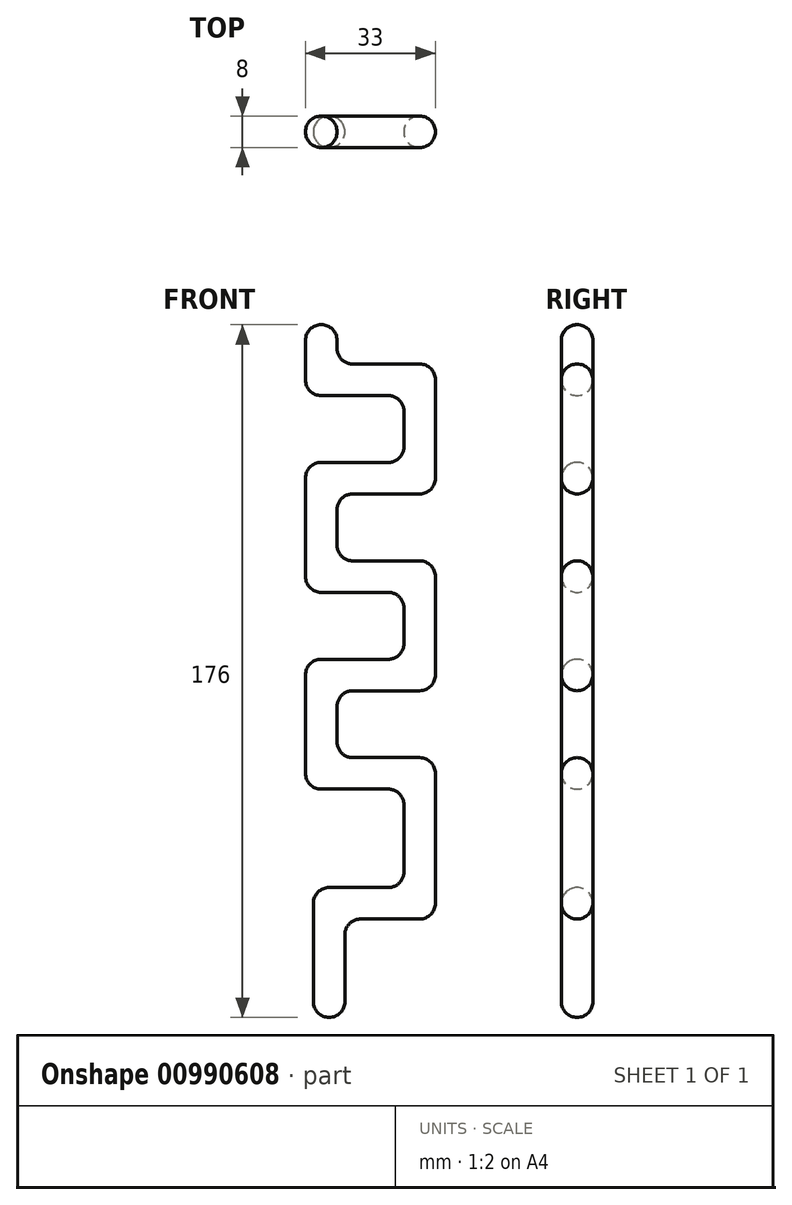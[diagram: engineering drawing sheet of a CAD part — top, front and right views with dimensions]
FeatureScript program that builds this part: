
annotation { "Feature Type Name" : "Feature", "Feature Type Description" : "" }
export const myFeature = defineFeature(function(context is Context, id is Id, definition is map)
    precondition{}
    {
        {
            var Q0;
            Q0=qCreatedBy(makeId("Top.planeOp"),FACE);
            var sketch = newSketch(context, id + "F0", { "sketchPlane" : qUnion([Q0])});
            skLineSegment(sketch, "E0.bottom", {"start": v(-57.93, 3.33) * mm, "end": v(-49.93, 3.33) * mm});
            skLineSegment(sketch, "E0.top", {"start": v(-57.93, -4.67) * mm, "end": v(-49.93, -4.67) * mm});
            skLineSegment(sketch, "E0.left", {"start": v(-57.93, 3.33) * mm, "end": v(-57.93, -4.67) * mm});
            skLineSegment(sketch, "E0.right", {"start": v(-49.93, 3.33) * mm, "end": v(-49.93, -4.67) * mm});
            skSolve(sketch);
        }
        {
            var Q0;
            Q0 = qSketchRegion(id + "F0", true);
            extrude(context, id + "F1", {"entities" : qUnion([Q0]), "depth" : 33 * mm, "offsetDistance" : 25 * mm});
        }
        {
            var Q0;
            Q0=makeQuery(id+"F1.opExtrude","SWEPT_FACE",FACE,{"disambiguationData":[OSD([sQuery(id+"F0.wireOp",EDGE,"E0.right")])]});
            var sketch = newSketch(context, id + "F2", { "sketchPlane" : qUnion([Q0])});
            skLineSegment(sketch, "E1.bottom", {"start": v(3.33, 33) * mm, "end": v(-4.67, 33) * mm});
            skLineSegment(sketch, "E1.top", {"start": v(3.33, 25) * mm, "end": v(-4.67, 25) * mm});
            skLineSegment(sketch, "E1.left", {"start": v(3.33, 33) * mm, "end": v(3.33, 25) * mm});
            skLineSegment(sketch, "E1.right", {"start": v(-4.67, 33) * mm, "end": v(-4.67, 25) * mm});
            skSolve(sketch);
        }
        {
            var Q0;
            Q0 = qSketchRegion(id + "F2", true);
            extrude(context, id + "F3", {"entities" : qUnion([Q0]), "operationType" : NewBodyOperationType.ADD, "depth" : 23 * mm, "offsetDistance" : 25 * mm});
        }
        {
            var Q0;
            Q0=makeQuery(id+"F3.opExtrude","SWEPT_FACE",FACE,{"disambiguationData":[OSD([sQuery(id+"F2.wireOp",EDGE,"E1.top")])]});
            var sketch = newSketch(context, id + "F4", { "sketchPlane" : qUnion([Q0])});
            skLineSegment(sketch, "E2.bottom", {"start": v(-26.93, 4.67) * mm, "end": v(-34.93, 4.67) * mm});
            skLineSegment(sketch, "E2.top", {"start": v(-26.93, -3.33) * mm, "end": v(-34.93, -3.33) * mm});
            skLineSegment(sketch, "E2.left", {"start": v(-26.93, 4.67) * mm, "end": v(-26.93, -3.33) * mm});
            skLineSegment(sketch, "E2.right", {"start": v(-34.93, 4.67) * mm, "end": v(-34.93, -3.33) * mm});
            skSolve(sketch);
        }
        {
            var Q0;
            Q0 = qSketchRegion(id + "F4", true);
            extrude(context, id + "F5", {"entities" : qUnion([Q0]), "operationType" : NewBodyOperationType.ADD, "oppositeDirection" : true, "depth" : 41 * mm, "offsetDistance" : 25 * mm});
        }
        {
            var Q0;
            Q0=makeQuery(id+"F5.opExtrude","SWEPT_FACE",FACE,{"disambiguationData":[OSD([sQuery(id+"F4.wireOp",EDGE,"E2.right")])]});
            var sketch = newSketch(context, id + "F6", { "sketchPlane" : qUnion([Q0])});
            skLineSegment(sketch, "E3.bottom", {"start": v(-3.33, 66) * mm, "end": v(4.67, 66) * mm});
            skLineSegment(sketch, "E3.top", {"start": v(-3.33, 58) * mm, "end": v(4.67, 58) * mm});
            skLineSegment(sketch, "E3.left", {"start": v(-3.33, 66) * mm, "end": v(-3.33, 58) * mm});
            skLineSegment(sketch, "E3.right", {"start": v(4.67, 66) * mm, "end": v(4.67, 58) * mm});
            skSolve(sketch);
        }
        {
            var Q0;
            Q0 = qSketchRegion(id + "F6", true);
            extrude(context, id + "F7", {"entities" : qUnion([Q0]), "operationType" : NewBodyOperationType.ADD, "depth" : 25 * mm, "offsetDistance" : 25 * mm});
        }
        {
            var Q0;
            Q0=makeQuery(id+"F7.boolean.opBoolean","MERGE",FACE,{"derivedFrom":[makeQuery(id+"F5.opExtrude","CAP_FACE",FACE,{"disambiguationData":[OSD([sQuery(id+"F4.wireOp",EDGE,"E2.bottom"),sQuery(id+"F4.wireOp",EDGE,"E2.top"),sQuery(id+"F4.wireOp",EDGE,"E2.left"),sQuery(id+"F4.wireOp",EDGE,"E2.right")])],"isStart":false}),makeQuery(id+"F7.opExtrude","SWEPT_FACE",FACE,{"disambiguationData":[OSD([sQuery(id+"F6.wireOp",EDGE,"E3.bottom")])]})]});
            var sketch = newSketch(context, id + "F8", { "sketchPlane" : qUnion([Q0])});
            skLineSegment(sketch, "E4.bottom", {"start": v(-59.93, -4.67) * mm, "end": v(-51.93, -4.67) * mm});
            skLineSegment(sketch, "E4.top", {"start": v(-59.93, 3.33) * mm, "end": v(-51.93, 3.33) * mm});
            skLineSegment(sketch, "E4.left", {"start": v(-59.93, -4.67) * mm, "end": v(-59.93, 3.33) * mm});
            skLineSegment(sketch, "E4.right", {"start": v(-51.93, -4.67) * mm, "end": v(-51.93, 3.33) * mm});
            skSolve(sketch);
        }
        {
            var Q0;
            Q0 = qSketchRegion(id + "F8", true);
            extrude(context, id + "F9", {"entities" : qUnion([Q0]), "operationType" : NewBodyOperationType.ADD, "depth" : 25 * mm, "offsetDistance" : 25 * mm});
        }
        {
            var Q0;
            Q0=makeQuery(id+"F9.opExtrude","SWEPT_FACE",FACE,{"disambiguationData":[OSD([sQuery(id+"F8.wireOp",EDGE,"E4.right")])]});
            var sketch = newSketch(context, id + "F10", { "sketchPlane" : qUnion([Q0])});
            skLineSegment(sketch, "E5.bottom", {"start": v(-4.67, 91) * mm, "end": v(3.33, 91) * mm});
            skLineSegment(sketch, "E5.top", {"start": v(-4.67, 83) * mm, "end": v(3.33, 83) * mm});
            skLineSegment(sketch, "E5.left", {"start": v(-4.67, 91) * mm, "end": v(-4.67, 83) * mm});
            skLineSegment(sketch, "E5.right", {"start": v(3.33, 91) * mm, "end": v(3.33, 83) * mm});
            skSolve(sketch);
        }
        {
            var Q0;
            Q0 = qSketchRegion(id + "F10", true);
            extrude(context, id + "F11", {"entities" : qUnion([Q0]), "operationType" : NewBodyOperationType.ADD, "depth" : 25 * mm, "offsetDistance" : 25 * mm});
        }
        {
            var Q0;
            Q0=makeQuery(id+"F11.boolean.opBoolean","MERGE",FACE,{"derivedFrom":[makeQuery(id+"F9.opExtrude","CAP_FACE",FACE,{"disambiguationData":[OSD([sQuery(id+"F8.wireOp",EDGE,"E4.bottom"),sQuery(id+"F8.wireOp",EDGE,"E4.top"),sQuery(id+"F8.wireOp",EDGE,"E4.left"),sQuery(id+"F8.wireOp",EDGE,"E4.right")])],"isStart":false}),makeQuery(id+"F11.opExtrude","SWEPT_FACE",FACE,{"disambiguationData":[OSD([sQuery(id+"F10.wireOp",EDGE,"E5.bottom")])]})]});
            var sketch = newSketch(context, id + "F12", { "sketchPlane" : qUnion([Q0])});
            skLineSegment(sketch, "E6.bottom", {"start": v(-26.93, 3.33) * mm, "end": v(-34.93, 3.33) * mm});
            skLineSegment(sketch, "E6.top", {"start": v(-26.93, -4.67) * mm, "end": v(-34.93, -4.67) * mm});
            skLineSegment(sketch, "E6.left", {"start": v(-26.93, 3.33) * mm, "end": v(-26.93, -4.67) * mm});
            skLineSegment(sketch, "E6.right", {"start": v(-34.93, 3.33) * mm, "end": v(-34.93, -4.67) * mm});
            skSolve(sketch);
        }
        {
            var Q0;
            Q0 = qSketchRegion(id + "F12", true);
            extrude(context, id + "F13", {"entities" : qUnion([Q0]), "operationType" : NewBodyOperationType.ADD, "depth" : 25 * mm, "offsetDistance" : 25 * mm});
        }
        {
            var Q0;
            Q0=makeQuery(id+"F13.opExtrude","SWEPT_FACE",FACE,{"disambiguationData":[OSD([sQuery(id+"F12.wireOp",EDGE,"E6.right")])]});
            var sketch = newSketch(context, id + "F14", { "sketchPlane" : qUnion([Q0])});
            skLineSegment(sketch, "E7.bottom", {"start": v(-3.33, 116) * mm, "end": v(4.67, 116) * mm});
            skLineSegment(sketch, "E7.top", {"start": v(-3.33, 108) * mm, "end": v(4.67, 108) * mm});
            skLineSegment(sketch, "E7.left", {"start": v(-3.33, 116) * mm, "end": v(-3.33, 108) * mm});
            skLineSegment(sketch, "E7.right", {"start": v(4.67, 116) * mm, "end": v(4.67, 108) * mm});
            skSolve(sketch);
        }
        {
            var Q0;
            Q0 = qSketchRegion(id + "F14", true);
            extrude(context, id + "F15", {"entities" : qUnion([Q0]), "operationType" : NewBodyOperationType.ADD, "depth" : 25 * mm, "offsetDistance" : 25 * mm});
        }
        {
            var Q0;
            Q0=makeQuery(id+"F15.boolean.opBoolean","MERGE",FACE,{"derivedFrom":[makeQuery(id+"F13.opExtrude","CAP_FACE",FACE,{"disambiguationData":[OSD([sQuery(id+"F12.wireOp",EDGE,"E6.bottom"),sQuery(id+"F12.wireOp",EDGE,"E6.top"),sQuery(id+"F12.wireOp",EDGE,"E6.left"),sQuery(id+"F12.wireOp",EDGE,"E6.right")])],"isStart":false}),makeQuery(id+"F15.opExtrude","SWEPT_FACE",FACE,{"disambiguationData":[OSD([sQuery(id+"F14.wireOp",EDGE,"E7.bottom")])]})]});
            var sketch = newSketch(context, id + "F16", { "sketchPlane" : qUnion([Q0])});
            skLineSegment(sketch, "E8.bottom", {"start": v(-59.93, -4.67) * mm, "end": v(-51.93, -4.67) * mm});
            skLineSegment(sketch, "E8.top", {"start": v(-59.93, 3.33) * mm, "end": v(-51.93, 3.33) * mm});
            skLineSegment(sketch, "E8.left", {"start": v(-59.93, -4.67) * mm, "end": v(-59.93, 3.33) * mm});
            skLineSegment(sketch, "E8.right", {"start": v(-51.93, -4.67) * mm, "end": v(-51.93, 3.33) * mm});
            skSolve(sketch);
        }
        {
            var Q0;
            Q0 = qSketchRegion(id + "F16", true);
            extrude(context, id + "F17", {"entities" : qUnion([Q0]), "operationType" : NewBodyOperationType.ADD, "depth" : 25 * mm, "offsetDistance" : 25 * mm});
        }
        {
            var Q0;
            Q0=makeQuery(id+"F17.opExtrude","SWEPT_FACE",FACE,{"disambiguationData":[OSD([sQuery(id+"F16.wireOp",EDGE,"E8.right")])]});
            var sketch = newSketch(context, id + "F18", { "sketchPlane" : qUnion([Q0])});
            skLineSegment(sketch, "E9.bottom", {"start": v(-4.67, 141) * mm, "end": v(3.33, 141) * mm});
            skLineSegment(sketch, "E9.top", {"start": v(-4.67, 133) * mm, "end": v(3.33, 133) * mm});
            skLineSegment(sketch, "E9.left", {"start": v(-4.67, 141) * mm, "end": v(-4.67, 133) * mm});
            skLineSegment(sketch, "E9.right", {"start": v(3.33, 141) * mm, "end": v(3.33, 133) * mm});
            skSolve(sketch);
        }
        {
            var Q0;
            Q0 = qSketchRegion(id + "F18", true);
            extrude(context, id + "F19", {"entities" : qUnion([Q0]), "operationType" : NewBodyOperationType.ADD, "depth" : 25 * mm, "offsetDistance" : 25 * mm});
        }
        {
            var Q0;
            Q0=makeQuery(id+"F19.boolean.opBoolean","MERGE",FACE,{"derivedFrom":[makeQuery(id+"F17.opExtrude","CAP_FACE",FACE,{"disambiguationData":[OSD([sQuery(id+"F16.wireOp",EDGE,"E8.bottom"),sQuery(id+"F16.wireOp",EDGE,"E8.top"),sQuery(id+"F16.wireOp",EDGE,"E8.left"),sQuery(id+"F16.wireOp",EDGE,"E8.right")])],"isStart":false}),makeQuery(id+"F19.opExtrude","SWEPT_FACE",FACE,{"disambiguationData":[OSD([sQuery(id+"F18.wireOp",EDGE,"E9.bottom")])]})]});
            var sketch = newSketch(context, id + "F20", { "sketchPlane" : qUnion([Q0])});
            skLineSegment(sketch, "E10.bottom", {"start": v(-26.93, 3.33) * mm, "end": v(-34.93, 3.33) * mm});
            skLineSegment(sketch, "E10.top", {"start": v(-26.93, -4.67) * mm, "end": v(-34.93, -4.67) * mm});
            skLineSegment(sketch, "E10.left", {"start": v(-26.93, 3.33) * mm, "end": v(-26.93, -4.67) * mm});
            skLineSegment(sketch, "E10.right", {"start": v(-34.93, 3.33) * mm, "end": v(-34.93, -4.67) * mm});
            skSolve(sketch);
        }
        {
            var Q0;
            Q0 = qSketchRegion(id + "F20", true);
            extrude(context, id + "F21", {"entities" : qUnion([Q0]), "operationType" : NewBodyOperationType.ADD, "depth" : 25 * mm, "offsetDistance" : 25 * mm});
        }
        {
            var Q0;
            Q0=makeQuery(id+"F21.opExtrude","SWEPT_FACE",FACE,{"disambiguationData":[OSD([sQuery(id+"F20.wireOp",EDGE,"E10.right")])]});
            var sketch = newSketch(context, id + "F22", { "sketchPlane" : qUnion([Q0])});
            skLineSegment(sketch, "E11.bottom", {"start": v(4.67, 166) * mm, "end": v(-3.33, 166) * mm});
            skLineSegment(sketch, "E11.top", {"start": v(4.67, 158) * mm, "end": v(-3.33, 158) * mm});
            skLineSegment(sketch, "E11.left", {"start": v(4.67, 166) * mm, "end": v(4.67, 158) * mm});
            skLineSegment(sketch, "E11.right", {"start": v(-3.33, 166) * mm, "end": v(-3.33, 158) * mm});
            skSolve(sketch);
        }
        {
            var Q0;
            Q0 = qSketchRegion(id + "F22", true);
            extrude(context, id + "F23", {"entities" : qUnion([Q0]), "operationType" : NewBodyOperationType.ADD, "depth" : 25 * mm, "offsetDistance" : 25 * mm});
        }
        {
            var Q0;
            Q0=makeQuery(id+"F23.boolean.opBoolean","MERGE",FACE,{"derivedFrom":[makeQuery(id+"F21.opExtrude","CAP_FACE",FACE,{"disambiguationData":[OSD([sQuery(id+"F20.wireOp",EDGE,"E10.bottom"),sQuery(id+"F20.wireOp",EDGE,"E10.top"),sQuery(id+"F20.wireOp",EDGE,"E10.left"),sQuery(id+"F20.wireOp",EDGE,"E10.right")])],"isStart":false}),makeQuery(id+"F23.opExtrude","SWEPT_FACE",FACE,{"disambiguationData":[OSD([sQuery(id+"F22.wireOp",EDGE,"E11.bottom")])]})]});
            var sketch = newSketch(context, id + "F24", { "sketchPlane" : qUnion([Q0])});
            skLineSegment(sketch, "E12.bottom", {"start": v(-59.93, -4.67) * mm, "end": v(-51.93, -4.67) * mm});
            skLineSegment(sketch, "E12.top", {"start": v(-59.93, 3.33) * mm, "end": v(-51.93, 3.33) * mm});
            skLineSegment(sketch, "E12.left", {"start": v(-59.93, -4.67) * mm, "end": v(-59.93, 3.33) * mm});
            skLineSegment(sketch, "E12.right", {"start": v(-51.93, -4.67) * mm, "end": v(-51.93, 3.33) * mm});
            skSolve(sketch);
        }
        {
            var Q0;
            Q0 = qSketchRegion(id + "F24", true);
            extrude(context, id + "F25", {"entities" : qUnion([Q0]), "operationType" : NewBodyOperationType.ADD, "depth" : 10 * mm, "offsetDistance" : 25 * mm});
        }
        {
            var Q0;
            Q0=makeQuery(id+"F3.opExtrude","SWEPT_EDGE",EDGE,{"disambiguationData":[OSD([sQuery(id+"F0.wireOp",EDGE,"E0.bottom"),sQuery(id+"F0.wireOp",EDGE,"E0.right"),sQuery(id+"F2.wireOp",EDGE,"E1.top"),sQuery(id+"F2.wireOp",EDGE,"E1.left")])]});
            var Q1;
            Q1=makeQuery(id+"F3.boolean.opBoolean","MERGE",EDGE,{"derivedFrom":[makeQuery(id+"F1.opExtrude","CAP_EDGE",EDGE,{"disambiguationData":[OSD([sQuery(id+"F0.wireOp",EDGE,"E0.top")])],"isStart":false}),makeQuery(id+"F3.opExtrude","SWEPT_EDGE",EDGE,{"disambiguationData":[OSD([sQuery(id+"F2.wireOp",EDGE,"E1.bottom"),sQuery(id+"F2.wireOp",EDGE,"E1.right")])]})]});
            var Q2;
            Q2=makeQuery(id+"F13.boolean.opBoolean","MERGE",FACE,{"derivedFrom":[makeQuery(id+"F11.opExtrude","CAP_FACE",FACE,{"disambiguationData":[OSD([sQuery(id+"F10.wireOp",EDGE,"E5.bottom"),sQuery(id+"F10.wireOp",EDGE,"E5.top"),sQuery(id+"F10.wireOp",EDGE,"E5.left"),sQuery(id+"F10.wireOp",EDGE,"E5.right")])],"isStart":false}),makeQuery(id+"F13.opExtrude","SWEPT_FACE",FACE,{"disambiguationData":[OSD([sQuery(id+"F12.wireOp",EDGE,"E6.left")])]})]});
            var Q3;
            Q3=makeQuery(id+"F13.opExtrude","SWEPT_EDGE",EDGE,{"disambiguationData":[OSD([sQuery(id+"F8.wireOp",EDGE,"E4.bottom"),sQuery(id+"F10.wireOp",EDGE,"E5.bottom"),sQuery(id+"F10.wireOp",EDGE,"E5.left"),sQuery(id+"F12.wireOp",EDGE,"E6.top"),sQuery(id+"F12.wireOp",EDGE,"E6.right")])]});
            var Q4;
            Q4=makeQuery(id+"F17.boolean.opBoolean","MERGE",FACE,{"derivedFrom":[makeQuery(id+"F15.opExtrude","CAP_FACE",FACE,{"disambiguationData":[OSD([sQuery(id+"F14.wireOp",EDGE,"E7.bottom"),sQuery(id+"F14.wireOp",EDGE,"E7.top"),sQuery(id+"F14.wireOp",EDGE,"E7.left"),sQuery(id+"F14.wireOp",EDGE,"E7.right")])],"isStart":false}),makeQuery(id+"F17.opExtrude","SWEPT_FACE",FACE,{"disambiguationData":[OSD([sQuery(id+"F16.wireOp",EDGE,"E8.left")])]})]});
            var Q5;
            Q5=makeQuery(id+"F7.opExtrude","SWEPT_EDGE",EDGE,{"disambiguationData":[OSD([sQuery(id+"F0.wireOp",EDGE,"E0.top"),sQuery(id+"F0.wireOp",EDGE,"E0.right"),sQuery(id+"F2.wireOp",EDGE,"E1.top"),sQuery(id+"F2.wireOp",EDGE,"E1.right"),sQuery(id+"F4.wireOp",EDGE,"E2.bottom"),sQuery(id+"F4.wireOp",EDGE,"E2.right"),sQuery(id+"F6.wireOp",EDGE,"E3.top"),sQuery(id+"F6.wireOp",EDGE,"E3.right")])]});
            var Q6;
            Q6=makeQuery(id+"F15.boolean.opBoolean","MERGE",EDGE,{"derivedFrom":[makeQuery(id+"F13.opExtrude","CAP_EDGE",EDGE,{"disambiguationData":[OSD([sQuery(id+"F12.wireOp",EDGE,"E6.top")])],"isStart":false}),makeQuery(id+"F15.opExtrude","SWEPT_EDGE",EDGE,{"disambiguationData":[OSD([sQuery(id+"F14.wireOp",EDGE,"E7.bottom"),sQuery(id+"F14.wireOp",EDGE,"E7.right")])]})]});
            var Q7;
            Q7=makeQuery(id+"F9.boolean.opBoolean","MERGE",FACE,{"derivedFrom":[makeQuery(id+"F7.opExtrude","CAP_FACE",FACE,{"disambiguationData":[OSD([sQuery(id+"F6.wireOp",EDGE,"E3.bottom"),sQuery(id+"F6.wireOp",EDGE,"E3.top"),sQuery(id+"F6.wireOp",EDGE,"E3.left"),sQuery(id+"F6.wireOp",EDGE,"E3.right")])],"isStart":false}),makeQuery(id+"F9.opExtrude","SWEPT_FACE",FACE,{"disambiguationData":[OSD([sQuery(id+"F8.wireOp",EDGE,"E4.left")])]})]});
            var Q8;
            Q8=makeQuery(id+"F7.opExtrude","SWEPT_FACE",FACE,{"disambiguationData":[OSD([sQuery(id+"F6.wireOp",EDGE,"E3.top")])]});
            var Q9;
            Q9=makeQuery(id+"F25.opExtrude","SWEPT_EDGE",EDGE,{"disambiguationData":[OSD([sQuery(id+"F20.wireOp",EDGE,"E10.top"),sQuery(id+"F22.wireOp",EDGE,"E11.bottom"),sQuery(id+"F22.wireOp",EDGE,"E11.left"),sQuery(id+"F24.wireOp",EDGE,"E12.bottom"),sQuery(id+"F24.wireOp",EDGE,"E12.right")])]});
            var Q10;
            Q10=makeQuery(id+"F25.opExtrude","SWEPT_EDGE",EDGE,{"disambiguationData":[OSD([sQuery(id+"F20.wireOp",EDGE,"E10.bottom"),sQuery(id+"F22.wireOp",EDGE,"E11.bottom"),sQuery(id+"F22.wireOp",EDGE,"E11.right"),sQuery(id+"F24.wireOp",EDGE,"E12.top"),sQuery(id+"F24.wireOp",EDGE,"E12.right")])]});
            var Q11;
            Q11=makeQuery(id+"F11.boolean.opBoolean","MERGE",EDGE,{"derivedFrom":[makeQuery(id+"F9.opExtrude","CAP_EDGE",EDGE,{"disambiguationData":[OSD([sQuery(id+"F8.wireOp",EDGE,"E4.bottom")])],"isStart":false}),makeQuery(id+"F11.opExtrude","SWEPT_EDGE",EDGE,{"disambiguationData":[OSD([sQuery(id+"F10.wireOp",EDGE,"E5.bottom"),sQuery(id+"F10.wireOp",EDGE,"E5.left")])]})]});
            var Q12;
            Q12=makeQuery(id+"F21.boolean.opBoolean","MERGE",EDGE,{"derivedFrom":[makeQuery(id+"F19.opExtrude","CAP_EDGE",EDGE,{"disambiguationData":[OSD([sQuery(id+"F18.wireOp",EDGE,"E9.right")])],"isStart":false}),makeQuery(id+"F21.opExtrude","SWEPT_EDGE",EDGE,{"disambiguationData":[OSD([sQuery(id+"F20.wireOp",EDGE,"E10.bottom"),sQuery(id+"F20.wireOp",EDGE,"E10.left")])]})]});
            var Q13;
            Q13=makeQuery(id+"F21.boolean.opBoolean","MERGE",FACE,{"derivedFrom":[makeQuery(id+"F19.opExtrude","CAP_FACE",FACE,{"disambiguationData":[OSD([sQuery(id+"F18.wireOp",EDGE,"E9.bottom"),sQuery(id+"F18.wireOp",EDGE,"E9.top"),sQuery(id+"F18.wireOp",EDGE,"E9.left"),sQuery(id+"F18.wireOp",EDGE,"E9.right")])],"isStart":false}),makeQuery(id+"F21.opExtrude","SWEPT_FACE",FACE,{"disambiguationData":[OSD([sQuery(id+"F20.wireOp",EDGE,"E10.left")])]})]});
            var Q14;
            Q14=makeQuery(id+"F21.opExtrude","SWEPT_FACE",FACE,{"disambiguationData":[OSD([sQuery(id+"F20.wireOp",EDGE,"E10.right")])]});
            var Q15;
            Q15=makeQuery(id+"F9.opExtrude","SWEPT_EDGE",EDGE,{"disambiguationData":[OSD([sQuery(id+"F4.wireOp",EDGE,"E2.bottom"),sQuery(id+"F6.wireOp",EDGE,"E3.bottom"),sQuery(id+"F6.wireOp",EDGE,"E3.right"),sQuery(id+"F8.wireOp",EDGE,"E4.bottom"),sQuery(id+"F8.wireOp",EDGE,"E4.right")])]});
            var Q16;
            Q16=makeQuery(id+"F17.opExtrude","SWEPT_EDGE",EDGE,{"disambiguationData":[OSD([sQuery(id+"F12.wireOp",EDGE,"E6.top"),sQuery(id+"F14.wireOp",EDGE,"E7.bottom"),sQuery(id+"F14.wireOp",EDGE,"E7.right"),sQuery(id+"F16.wireOp",EDGE,"E8.bottom"),sQuery(id+"F16.wireOp",EDGE,"E8.right")])]});
            var Q17;
            Q17=makeQuery(id+"F5.opExtrude","SWEPT_FACE",FACE,{"disambiguationData":[OSD([sQuery(id+"F4.wireOp",EDGE,"E2.right")])]});
            var Q18;
            Q18=makeQuery(id+"F19.boolean.opBoolean","MERGE",EDGE,{"derivedFrom":[makeQuery(id+"F17.opExtrude","CAP_EDGE",EDGE,{"disambiguationData":[OSD([sQuery(id+"F16.wireOp",EDGE,"E8.bottom")])],"isStart":false}),makeQuery(id+"F19.opExtrude","SWEPT_EDGE",EDGE,{"disambiguationData":[OSD([sQuery(id+"F18.wireOp",EDGE,"E9.bottom"),sQuery(id+"F18.wireOp",EDGE,"E9.left")])]})]});
            var Q19;
            Q19=makeQuery(id+"F15.opExtrude","SWEPT_EDGE",EDGE,{"disambiguationData":[OSD([sQuery(id+"F8.wireOp",EDGE,"E4.bottom"),sQuery(id+"F10.wireOp",EDGE,"E5.bottom"),sQuery(id+"F10.wireOp",EDGE,"E5.left"),sQuery(id+"F12.wireOp",EDGE,"E6.top"),sQuery(id+"F12.wireOp",EDGE,"E6.right"),sQuery(id+"F14.wireOp",EDGE,"E7.top"),sQuery(id+"F14.wireOp",EDGE,"E7.right")])]});
            var Q20;
            Q20=makeQuery(id+"F11.opExtrude","SWEPT_FACE",FACE,{"disambiguationData":[OSD([sQuery(id+"F10.wireOp",EDGE,"E5.top")])]});
            var Q21;
            Q21=makeQuery(id+"F5.opExtrude","SWEPT_EDGE",EDGE,{"disambiguationData":[OSD([sQuery(id+"F0.wireOp",EDGE,"E0.top"),sQuery(id+"F0.wireOp",EDGE,"E0.right"),sQuery(id+"F2.wireOp",EDGE,"E1.top"),sQuery(id+"F2.wireOp",EDGE,"E1.right"),sQuery(id+"F4.wireOp",EDGE,"E2.bottom"),sQuery(id+"F4.wireOp",EDGE,"E2.right")])]});
            var Q22;
            Q22=makeQuery(id+"F3.opExtrude","SWEPT_EDGE",EDGE,{"disambiguationData":[OSD([sQuery(id+"F0.wireOp",EDGE,"E0.top"),sQuery(id+"F0.wireOp",EDGE,"E0.right"),sQuery(id+"F2.wireOp",EDGE,"E1.top"),sQuery(id+"F2.wireOp",EDGE,"E1.right")])]});
            var Q23;
            Q23=makeQuery(id+"F23.opExtrude","SWEPT_FACE",FACE,{"disambiguationData":[OSD([sQuery(id+"F22.wireOp",EDGE,"E11.top")])]});
            var Q24;
            Q24=makeQuery(id+"F25.opExtrude","SWEPT_FACE",FACE,{"disambiguationData":[OSD([sQuery(id+"F24.wireOp",EDGE,"E12.right")])]});
            var Q25;
            Q25=makeQuery(id+"F19.opExtrude","SWEPT_EDGE",EDGE,{"disambiguationData":[OSD([sQuery(id+"F12.wireOp",EDGE,"E6.bottom"),sQuery(id+"F14.wireOp",EDGE,"E7.bottom"),sQuery(id+"F14.wireOp",EDGE,"E7.left"),sQuery(id+"F16.wireOp",EDGE,"E8.top"),sQuery(id+"F16.wireOp",EDGE,"E8.right"),sQuery(id+"F18.wireOp",EDGE,"E9.top"),sQuery(id+"F18.wireOp",EDGE,"E9.right")])]});
            var Q26;
            Q26=makeQuery(id+"F13.opExtrude","SWEPT_FACE",FACE,{"disambiguationData":[OSD([sQuery(id+"F12.wireOp",EDGE,"E6.right")])]});
            var Q27;
            Q27=makeQuery(id+"F5.boolean.opBoolean","MERGE",FACE,{"derivedFrom":[makeQuery(id+"F3.opExtrude","CAP_FACE",FACE,{"disambiguationData":[OSD([sQuery(id+"F2.wireOp",EDGE,"E1.bottom"),sQuery(id+"F2.wireOp",EDGE,"E1.top"),sQuery(id+"F2.wireOp",EDGE,"E1.left"),sQuery(id+"F2.wireOp",EDGE,"E1.right")])],"isStart":false}),makeQuery(id+"F5.opExtrude","SWEPT_FACE",FACE,{"disambiguationData":[OSD([sQuery(id+"F4.wireOp",EDGE,"E2.left")])]})]});
            var Q28;
            Q28=makeQuery(id+"F23.boolean.opBoolean","MERGE",FACE,{"derivedFrom":[makeQuery(id+"F21.opExtrude","CAP_FACE",FACE,{"disambiguationData":[OSD([sQuery(id+"F20.wireOp",EDGE,"E10.bottom"),sQuery(id+"F20.wireOp",EDGE,"E10.top"),sQuery(id+"F20.wireOp",EDGE,"E10.left"),sQuery(id+"F20.wireOp",EDGE,"E10.right")])],"isStart":false}),makeQuery(id+"F23.opExtrude","SWEPT_FACE",FACE,{"disambiguationData":[OSD([sQuery(id+"F22.wireOp",EDGE,"E11.bottom")])]})]});
            var Q29;
            Q29=makeQuery(id+"F25.boolean.opBoolean","MERGE",FACE,{"derivedFrom":[makeQuery(id+"F23.opExtrude","CAP_FACE",FACE,{"disambiguationData":[OSD([sQuery(id+"F22.wireOp",EDGE,"E11.bottom"),sQuery(id+"F22.wireOp",EDGE,"E11.top"),sQuery(id+"F22.wireOp",EDGE,"E11.left"),sQuery(id+"F22.wireOp",EDGE,"E11.right")])],"isStart":false}),makeQuery(id+"F25.opExtrude","SWEPT_FACE",FACE,{"disambiguationData":[OSD([sQuery(id+"F24.wireOp",EDGE,"E12.left")])]})]});
            var Q30;
            Q30=makeQuery(id+"F15.opExtrude","SWEPT_FACE",FACE,{"disambiguationData":[OSD([sQuery(id+"F14.wireOp",EDGE,"E7.top")])]});
            var Q31;
            Q31=makeQuery(id+"F11.boolean.opBoolean","MERGE",FACE,{"derivedFrom":[makeQuery(id+"F9.opExtrude","CAP_FACE",FACE,{"disambiguationData":[OSD([sQuery(id+"F8.wireOp",EDGE,"E4.bottom"),sQuery(id+"F8.wireOp",EDGE,"E4.top"),sQuery(id+"F8.wireOp",EDGE,"E4.left"),sQuery(id+"F8.wireOp",EDGE,"E4.right")])],"isStart":false}),makeQuery(id+"F11.opExtrude","SWEPT_FACE",FACE,{"disambiguationData":[OSD([sQuery(id+"F10.wireOp",EDGE,"E5.bottom")])]})]});
            var Q32;
            Q32=makeQuery(id+"F15.boolean.opBoolean","MERGE",FACE,{"derivedFrom":[makeQuery(id+"F13.opExtrude","CAP_FACE",FACE,{"disambiguationData":[OSD([sQuery(id+"F12.wireOp",EDGE,"E6.bottom"),sQuery(id+"F12.wireOp",EDGE,"E6.top"),sQuery(id+"F12.wireOp",EDGE,"E6.left"),sQuery(id+"F12.wireOp",EDGE,"E6.right")])],"isStart":false}),makeQuery(id+"F15.opExtrude","SWEPT_FACE",FACE,{"disambiguationData":[OSD([sQuery(id+"F14.wireOp",EDGE,"E7.bottom")])]})]});
            var Q33;
            Q33=makeQuery(id+"F25.boolean.opBoolean","MERGE",EDGE,{"derivedFrom":[makeQuery(id+"F23.opExtrude","CAP_EDGE",EDGE,{"disambiguationData":[OSD([sQuery(id+"F22.wireOp",EDGE,"E11.left")])],"isStart":false}),makeQuery(id+"F25.opExtrude","SWEPT_EDGE",EDGE,{"disambiguationData":[OSD([sQuery(id+"F24.wireOp",EDGE,"E12.bottom"),sQuery(id+"F24.wireOp",EDGE,"E12.left")])]})]});
            var Q34;
            Q34=makeQuery(id+"F9.opExtrude","SWEPT_EDGE",EDGE,{"disambiguationData":[OSD([sQuery(id+"F4.wireOp",EDGE,"E2.top"),sQuery(id+"F6.wireOp",EDGE,"E3.bottom"),sQuery(id+"F6.wireOp",EDGE,"E3.left"),sQuery(id+"F8.wireOp",EDGE,"E4.top"),sQuery(id+"F8.wireOp",EDGE,"E4.right")])]});
            var Q35;
            Q35=makeQuery(id+"F7.boolean.opBoolean","MERGE",FACE,{"derivedFrom":[makeQuery(id+"F5.opExtrude","CAP_FACE",FACE,{"disambiguationData":[OSD([sQuery(id+"F4.wireOp",EDGE,"E2.bottom"),sQuery(id+"F4.wireOp",EDGE,"E2.top"),sQuery(id+"F4.wireOp",EDGE,"E2.left"),sQuery(id+"F4.wireOp",EDGE,"E2.right")])],"isStart":false}),makeQuery(id+"F7.opExtrude","SWEPT_FACE",FACE,{"disambiguationData":[OSD([sQuery(id+"F6.wireOp",EDGE,"E3.bottom")])]})]});
            var Q36;
            Q36=makeQuery(id+"F19.opExtrude","SWEPT_EDGE",EDGE,{"disambiguationData":[OSD([sQuery(id+"F12.wireOp",EDGE,"E6.top"),sQuery(id+"F14.wireOp",EDGE,"E7.bottom"),sQuery(id+"F14.wireOp",EDGE,"E7.right"),sQuery(id+"F16.wireOp",EDGE,"E8.bottom"),sQuery(id+"F16.wireOp",EDGE,"E8.right"),sQuery(id+"F18.wireOp",EDGE,"E9.top"),sQuery(id+"F18.wireOp",EDGE,"E9.left")])]});
            var Q37;
            Q37=makeQuery(id+"F7.boolean.opBoolean","MERGE",EDGE,{"derivedFrom":[makeQuery(id+"F5.opExtrude","CAP_EDGE",EDGE,{"disambiguationData":[OSD([sQuery(id+"F4.wireOp",EDGE,"E2.bottom")])],"isStart":false}),makeQuery(id+"F7.opExtrude","SWEPT_EDGE",EDGE,{"disambiguationData":[OSD([sQuery(id+"F6.wireOp",EDGE,"E3.bottom"),sQuery(id+"F6.wireOp",EDGE,"E3.right")])]})]});
            var Q38;
            Q38=makeQuery(id+"F5.boolean.opBoolean","MERGE",EDGE,{"derivedFrom":[makeQuery(id+"F3.opExtrude","CAP_EDGE",EDGE,{"disambiguationData":[OSD([sQuery(id+"F2.wireOp",EDGE,"E1.left")])],"isStart":false}),makeQuery(id+"F5.opExtrude","SWEPT_EDGE",EDGE,{"disambiguationData":[OSD([sQuery(id+"F4.wireOp",EDGE,"E2.top"),sQuery(id+"F4.wireOp",EDGE,"E2.left")])]})]});
            var Q39;
            Q39=makeQuery(id+"F23.boolean.opBoolean","MERGE",EDGE,{"derivedFrom":[makeQuery(id+"F21.opExtrude","CAP_EDGE",EDGE,{"disambiguationData":[OSD([sQuery(id+"F20.wireOp",EDGE,"E10.top")])],"isStart":false}),makeQuery(id+"F23.opExtrude","SWEPT_EDGE",EDGE,{"disambiguationData":[OSD([sQuery(id+"F22.wireOp",EDGE,"E11.bottom"),sQuery(id+"F22.wireOp",EDGE,"E11.left")])]})]});
            var Q40;
            Q40=makeQuery(id+"F5.boolean.opBoolean","MERGE",EDGE,{"derivedFrom":[makeQuery(id+"F3.opExtrude","CAP_EDGE",EDGE,{"disambiguationData":[OSD([sQuery(id+"F2.wireOp",EDGE,"E1.right")])],"isStart":false}),makeQuery(id+"F5.opExtrude","SWEPT_EDGE",EDGE,{"disambiguationData":[OSD([sQuery(id+"F4.wireOp",EDGE,"E2.bottom"),sQuery(id+"F4.wireOp",EDGE,"E2.left")])]})]});
            var Q41;
            Q41=makeQuery(id+"F17.opExtrude","SWEPT_EDGE",EDGE,{"disambiguationData":[OSD([sQuery(id+"F12.wireOp",EDGE,"E6.bottom"),sQuery(id+"F14.wireOp",EDGE,"E7.bottom"),sQuery(id+"F14.wireOp",EDGE,"E7.left"),sQuery(id+"F16.wireOp",EDGE,"E8.top"),sQuery(id+"F16.wireOp",EDGE,"E8.right")])]});
            var Q42;
            Q42=makeQuery(id+"F3.opExtrude","SWEPT_FACE",FACE,{"disambiguationData":[OSD([sQuery(id+"F2.wireOp",EDGE,"E1.top")])]});
            var Q43;
            Q43=makeQuery(id+"F9.opExtrude","SWEPT_FACE",FACE,{"disambiguationData":[OSD([sQuery(id+"F8.wireOp",EDGE,"E4.right")])]});
            var Q44;
            Q44=makeQuery(id+"F11.opExtrude","SWEPT_EDGE",EDGE,{"disambiguationData":[OSD([sQuery(id+"F4.wireOp",EDGE,"E2.bottom"),sQuery(id+"F6.wireOp",EDGE,"E3.bottom"),sQuery(id+"F6.wireOp",EDGE,"E3.right"),sQuery(id+"F8.wireOp",EDGE,"E4.bottom"),sQuery(id+"F8.wireOp",EDGE,"E4.right"),sQuery(id+"F10.wireOp",EDGE,"E5.top"),sQuery(id+"F10.wireOp",EDGE,"E5.left")])]});
            var Q45;
            Q45=makeQuery(id+"F19.boolean.opBoolean","MERGE",FACE,{"derivedFrom":[makeQuery(id+"F17.opExtrude","CAP_FACE",FACE,{"disambiguationData":[OSD([sQuery(id+"F16.wireOp",EDGE,"E8.bottom"),sQuery(id+"F16.wireOp",EDGE,"E8.top"),sQuery(id+"F16.wireOp",EDGE,"E8.left"),sQuery(id+"F16.wireOp",EDGE,"E8.right")])],"isStart":false}),makeQuery(id+"F19.opExtrude","SWEPT_FACE",FACE,{"disambiguationData":[OSD([sQuery(id+"F18.wireOp",EDGE,"E9.bottom")])]})]});
            var Q46;
            Q46=makeQuery(id+"F19.opExtrude","SWEPT_FACE",FACE,{"disambiguationData":[OSD([sQuery(id+"F18.wireOp",EDGE,"E9.top")])]});
            var Q47;
            Q47=makeQuery(id+"F17.opExtrude","SWEPT_FACE",FACE,{"disambiguationData":[OSD([sQuery(id+"F16.wireOp",EDGE,"E8.right")])]});
            var Q48;
            Q48=makeQuery(id+"F3.boolean.opBoolean","MERGE",FACE,{"derivedFrom":[makeQuery(id+"F1.opExtrude","CAP_FACE",FACE,{"disambiguationData":[OSD([sQuery(id+"F0.wireOp",EDGE,"E0.bottom"),sQuery(id+"F0.wireOp",EDGE,"E0.top"),sQuery(id+"F0.wireOp",EDGE,"E0.left"),sQuery(id+"F0.wireOp",EDGE,"E0.right")])],"isStart":false}),makeQuery(id+"F3.opExtrude","SWEPT_FACE",FACE,{"disambiguationData":[OSD([sQuery(id+"F2.wireOp",EDGE,"E1.bottom")])]})]});
            var Q49;
            Q49=makeQuery(id+"F11.opExtrude","SWEPT_EDGE",EDGE,{"disambiguationData":[OSD([sQuery(id+"F4.wireOp",EDGE,"E2.top"),sQuery(id+"F6.wireOp",EDGE,"E3.bottom"),sQuery(id+"F6.wireOp",EDGE,"E3.left"),sQuery(id+"F8.wireOp",EDGE,"E4.top"),sQuery(id+"F8.wireOp",EDGE,"E4.right"),sQuery(id+"F10.wireOp",EDGE,"E5.top"),sQuery(id+"F10.wireOp",EDGE,"E5.right")])]});
            var Q50;
            Q50=makeQuery(id+"F23.opExtrude","SWEPT_EDGE",EDGE,{"disambiguationData":[OSD([sQuery(id+"F16.wireOp",EDGE,"E8.bottom"),sQuery(id+"F18.wireOp",EDGE,"E9.bottom"),sQuery(id+"F18.wireOp",EDGE,"E9.left"),sQuery(id+"F20.wireOp",EDGE,"E10.top"),sQuery(id+"F20.wireOp",EDGE,"E10.right"),sQuery(id+"F22.wireOp",EDGE,"E11.top"),sQuery(id+"F22.wireOp",EDGE,"E11.left")])]});
            var Q51;
            Q51=makeQuery(id+"F7.boolean.opBoolean","MERGE",EDGE,{"derivedFrom":[makeQuery(id+"F5.opExtrude","CAP_EDGE",EDGE,{"disambiguationData":[OSD([sQuery(id+"F4.wireOp",EDGE,"E2.top")])],"isStart":false}),makeQuery(id+"F7.opExtrude","SWEPT_EDGE",EDGE,{"disambiguationData":[OSD([sQuery(id+"F6.wireOp",EDGE,"E3.bottom"),sQuery(id+"F6.wireOp",EDGE,"E3.left")])]})]});
            var Q52;
            Q52=makeQuery(id+"F25.boolean.opBoolean","MERGE",EDGE,{"derivedFrom":[makeQuery(id+"F23.opExtrude","CAP_EDGE",EDGE,{"disambiguationData":[OSD([sQuery(id+"F22.wireOp",EDGE,"E11.right")])],"isStart":false}),makeQuery(id+"F25.opExtrude","SWEPT_EDGE",EDGE,{"disambiguationData":[OSD([sQuery(id+"F24.wireOp",EDGE,"E12.top"),sQuery(id+"F24.wireOp",EDGE,"E12.left")])]})]});
            var Q53;
            Q53=makeQuery(id+"F19.boolean.opBoolean","MERGE",EDGE,{"derivedFrom":[makeQuery(id+"F17.opExtrude","CAP_EDGE",EDGE,{"disambiguationData":[OSD([sQuery(id+"F16.wireOp",EDGE,"E8.top")])],"isStart":false}),makeQuery(id+"F19.opExtrude","SWEPT_EDGE",EDGE,{"disambiguationData":[OSD([sQuery(id+"F18.wireOp",EDGE,"E9.bottom"),sQuery(id+"F18.wireOp",EDGE,"E9.right")])]})]});
            var Q54;
            Q54=makeQuery(id+"F9.opExtrude","CAP_EDGE",EDGE,{"disambiguationData":[OSD([sQuery(id+"F8.wireOp",EDGE,"E4.left")])],"isStart":false});
            var Q55;
            Q55=makeQuery(id+"F3.opExtrude","CAP_EDGE",EDGE,{"disambiguationData":[OSD([sQuery(id+"F2.wireOp",EDGE,"E1.top")])],"isStart":false});
            var Q56;
            Q56=makeQuery(id+"F13.opExtrude","SWEPT_EDGE",EDGE,{"disambiguationData":[OSD([sQuery(id+"F8.wireOp",EDGE,"E4.top"),sQuery(id+"F10.wireOp",EDGE,"E5.bottom"),sQuery(id+"F10.wireOp",EDGE,"E5.right"),sQuery(id+"F12.wireOp",EDGE,"E6.bottom"),sQuery(id+"F12.wireOp",EDGE,"E6.right")])]});
            var Q57;
            Q57=makeQuery(id+"F7.opExtrude","CAP_EDGE",EDGE,{"disambiguationData":[OSD([sQuery(id+"F6.wireOp",EDGE,"E3.top")])],"isStart":false});
            var Q58;
            Q58=makeQuery(id+"F15.opExtrude","SWEPT_EDGE",EDGE,{"disambiguationData":[OSD([sQuery(id+"F8.wireOp",EDGE,"E4.top"),sQuery(id+"F10.wireOp",EDGE,"E5.bottom"),sQuery(id+"F10.wireOp",EDGE,"E5.right"),sQuery(id+"F12.wireOp",EDGE,"E6.bottom"),sQuery(id+"F12.wireOp",EDGE,"E6.right"),sQuery(id+"F14.wireOp",EDGE,"E7.top"),sQuery(id+"F14.wireOp",EDGE,"E7.left")])]});
            var Q59;
            Q59=makeQuery(id+"F5.boolean.opBoolean","INTERSECT",EDGE,{"derivedFrom":[makeQuery(id+"F3.boolean.opBoolean","MERGE",FACE,{"derivedFrom":[makeQuery(id+"F1.opExtrude","CAP_FACE",FACE,{"disambiguationData":[OSD([sQuery(id+"F0.wireOp",EDGE,"E0.bottom"),sQuery(id+"F0.wireOp",EDGE,"E0.top"),sQuery(id+"F0.wireOp",EDGE,"E0.left"),sQuery(id+"F0.wireOp",EDGE,"E0.right")])],"isStart":false}),makeQuery(id+"F3.opExtrude","SWEPT_FACE",FACE,{"disambiguationData":[OSD([sQuery(id+"F2.wireOp",EDGE,"E1.bottom")])]})]}),makeQuery(id+"F5.opExtrude","SWEPT_FACE",FACE,{"disambiguationData":[OSD([sQuery(id+"F4.wireOp",EDGE,"E2.right")])]})]});
            var Q60;
            Q60=makeQuery(id+"F17.boolean.opBoolean","MERGE",EDGE,{"derivedFrom":[makeQuery(id+"F15.opExtrude","CAP_EDGE",EDGE,{"disambiguationData":[OSD([sQuery(id+"F14.wireOp",EDGE,"E7.right")])],"isStart":false}),makeQuery(id+"F17.opExtrude","SWEPT_EDGE",EDGE,{"disambiguationData":[OSD([sQuery(id+"F16.wireOp",EDGE,"E8.bottom"),sQuery(id+"F16.wireOp",EDGE,"E8.left")])]})]});
            var Q61;
            Q61=makeQuery(id+"F25.opExtrude","CAP_EDGE",EDGE,{"disambiguationData":[OSD([sQuery(id+"F24.wireOp",EDGE,"E12.left")])],"isStart":false});
            var Q62;
            Q62=makeQuery(id+"F13.opExtrude","CAP_EDGE",EDGE,{"disambiguationData":[OSD([sQuery(id+"F12.wireOp",EDGE,"E6.left")])],"isStart":false});
            var Q63;
            Q63=makeQuery(id+"F21.opExtrude","CAP_EDGE",EDGE,{"disambiguationData":[OSD([sQuery(id+"F20.wireOp",EDGE,"E10.left")])],"isStart":false});
            var Q64;
            Q64=makeQuery(id+"F21.opExtrude","SWEPT_EDGE",EDGE,{"disambiguationData":[OSD([sQuery(id+"F16.wireOp",EDGE,"E8.bottom"),sQuery(id+"F18.wireOp",EDGE,"E9.bottom"),sQuery(id+"F18.wireOp",EDGE,"E9.left"),sQuery(id+"F20.wireOp",EDGE,"E10.top"),sQuery(id+"F20.wireOp",EDGE,"E10.right")])]});
            var Q65;
            Q65=makeQuery(id+"F5.opExtrude","CAP_EDGE",EDGE,{"disambiguationData":[OSD([sQuery(id+"F4.wireOp",EDGE,"E2.left")])],"isStart":false});
            var Q66;
            Q66=makeQuery(id+"F23.opExtrude","CAP_EDGE",EDGE,{"disambiguationData":[OSD([sQuery(id+"F22.wireOp",EDGE,"E11.top")])],"isStart":false});
            var Q67;
            Q67=makeQuery(id+"F15.opExtrude","CAP_EDGE",EDGE,{"disambiguationData":[OSD([sQuery(id+"F14.wireOp",EDGE,"E7.top")])],"isStart":false});
            var Q68;
            Q68=makeQuery(id+"F19.opExtrude","CAP_EDGE",EDGE,{"disambiguationData":[OSD([sQuery(id+"F18.wireOp",EDGE,"E9.top")])],"isStart":false});
            var Q69;
            Q69=makeQuery(id+"F11.boolean.opBoolean","MERGE",EDGE,{"derivedFrom":[makeQuery(id+"F9.opExtrude","CAP_EDGE",EDGE,{"disambiguationData":[OSD([sQuery(id+"F8.wireOp",EDGE,"E4.top")])],"isStart":false}),makeQuery(id+"F11.opExtrude","SWEPT_EDGE",EDGE,{"disambiguationData":[OSD([sQuery(id+"F10.wireOp",EDGE,"E5.bottom"),sQuery(id+"F10.wireOp",EDGE,"E5.right")])]})]});
            var Q70;
            Q70=makeQuery(id+"F11.opExtrude","CAP_EDGE",EDGE,{"disambiguationData":[OSD([sQuery(id+"F10.wireOp",EDGE,"E5.top")])],"isStart":true});
            var Q71;
            Q71=makeQuery(id+"F17.opExtrude","CAP_EDGE",EDGE,{"disambiguationData":[OSD([sQuery(id+"F16.wireOp",EDGE,"E8.right")])],"isStart":true});
            var Q72;
            Q72=makeQuery(id+"F21.opExtrude","CAP_EDGE",EDGE,{"disambiguationData":[OSD([sQuery(id+"F20.wireOp",EDGE,"E10.right")])],"isStart":true});
            var Q73;
            Q73=makeQuery(id+"F7.opExtrude","CAP_EDGE",EDGE,{"disambiguationData":[OSD([sQuery(id+"F6.wireOp",EDGE,"E3.top")])],"isStart":true});
            var Q74;
            Q74=makeQuery(id+"F3.boolean.opBoolean","MERGE",EDGE,{"derivedFrom":[makeQuery(id+"F1.opExtrude","CAP_EDGE",EDGE,{"disambiguationData":[OSD([sQuery(id+"F0.wireOp",EDGE,"E0.bottom")])],"isStart":false}),makeQuery(id+"F3.opExtrude","SWEPT_EDGE",EDGE,{"disambiguationData":[OSD([sQuery(id+"F2.wireOp",EDGE,"E1.bottom"),sQuery(id+"F2.wireOp",EDGE,"E1.left")])]})]});
            var Q75;
            Q75=makeQuery(id+"F21.opExtrude","SWEPT_EDGE",EDGE,{"disambiguationData":[OSD([sQuery(id+"F16.wireOp",EDGE,"E8.top"),sQuery(id+"F18.wireOp",EDGE,"E9.bottom"),sQuery(id+"F18.wireOp",EDGE,"E9.right"),sQuery(id+"F20.wireOp",EDGE,"E10.bottom"),sQuery(id+"F20.wireOp",EDGE,"E10.right")])]});
            var Q76;
            Q76=makeQuery(id+"F25.opExtrude","CAP_EDGE",EDGE,{"disambiguationData":[OSD([sQuery(id+"F24.wireOp",EDGE,"E12.bottom")])],"isStart":false});
            var Q77;
            Q77=makeQuery(id+"F25.opExtrude","CAP_EDGE",EDGE,{"disambiguationData":[OSD([sQuery(id+"F24.wireOp",EDGE,"E12.top")])],"isStart":false});
            var Q78;
            Q78=makeQuery(id+"F9.boolean.opBoolean","MERGE",EDGE,{"derivedFrom":[makeQuery(id+"F7.opExtrude","CAP_EDGE",EDGE,{"disambiguationData":[OSD([sQuery(id+"F6.wireOp",EDGE,"E3.left")])],"isStart":false}),makeQuery(id+"F9.opExtrude","SWEPT_EDGE",EDGE,{"disambiguationData":[OSD([sQuery(id+"F8.wireOp",EDGE,"E4.top"),sQuery(id+"F8.wireOp",EDGE,"E4.left")])]})]});
            var Q79;
            Q79=makeQuery(id+"F5.opExtrude","SWEPT_EDGE",EDGE,{"disambiguationData":[OSD([sQuery(id+"F0.wireOp",EDGE,"E0.bottom"),sQuery(id+"F0.wireOp",EDGE,"E0.right"),sQuery(id+"F2.wireOp",EDGE,"E1.top"),sQuery(id+"F2.wireOp",EDGE,"E1.left"),sQuery(id+"F4.wireOp",EDGE,"E2.top"),sQuery(id+"F4.wireOp",EDGE,"E2.right")])]});
            var Q80;
            Q80=makeQuery(id+"F7.opExtrude","SWEPT_EDGE",EDGE,{"disambiguationData":[OSD([sQuery(id+"F0.wireOp",EDGE,"E0.bottom"),sQuery(id+"F0.wireOp",EDGE,"E0.right"),sQuery(id+"F2.wireOp",EDGE,"E1.top"),sQuery(id+"F2.wireOp",EDGE,"E1.left"),sQuery(id+"F4.wireOp",EDGE,"E2.top"),sQuery(id+"F4.wireOp",EDGE,"E2.right"),sQuery(id+"F6.wireOp",EDGE,"E3.top"),sQuery(id+"F6.wireOp",EDGE,"E3.left")])]});
            var Q81;
            Q81=makeQuery(id+"F1.opExtrude","CAP_EDGE",EDGE,{"disambiguationData":[OSD([sQuery(id+"F0.wireOp",EDGE,"E0.left")])],"isStart":false});
            var Q82;
            Q82=makeQuery(id+"F15.opExtrude","CAP_EDGE",EDGE,{"disambiguationData":[OSD([sQuery(id+"F14.wireOp",EDGE,"E7.top")])],"isStart":true});
            var Q83;
            Q83=makeQuery(id+"F19.opExtrude","CAP_EDGE",EDGE,{"disambiguationData":[OSD([sQuery(id+"F18.wireOp",EDGE,"E9.top")])],"isStart":true});
            var Q84;
            Q84=makeQuery(id+"F15.boolean.opBoolean","MERGE",EDGE,{"derivedFrom":[makeQuery(id+"F13.opExtrude","CAP_EDGE",EDGE,{"disambiguationData":[OSD([sQuery(id+"F12.wireOp",EDGE,"E6.bottom")])],"isStart":false}),makeQuery(id+"F15.opExtrude","SWEPT_EDGE",EDGE,{"disambiguationData":[OSD([sQuery(id+"F14.wireOp",EDGE,"E7.bottom"),sQuery(id+"F14.wireOp",EDGE,"E7.left")])]})]});
            var Q85;
            Q85=makeQuery(id+"F11.opExtrude","CAP_EDGE",EDGE,{"disambiguationData":[OSD([sQuery(id+"F10.wireOp",EDGE,"E5.top")])],"isStart":false});
            var Q86;
            Q86=makeQuery(id+"F9.boolean.opBoolean","MERGE",EDGE,{"derivedFrom":[makeQuery(id+"F7.opExtrude","CAP_EDGE",EDGE,{"disambiguationData":[OSD([sQuery(id+"F6.wireOp",EDGE,"E3.right")])],"isStart":false}),makeQuery(id+"F9.opExtrude","SWEPT_EDGE",EDGE,{"disambiguationData":[OSD([sQuery(id+"F8.wireOp",EDGE,"E4.bottom"),sQuery(id+"F8.wireOp",EDGE,"E4.left")])]})]});
            var Q87;
            Q87=makeQuery(id+"F23.opExtrude","CAP_EDGE",EDGE,{"disambiguationData":[OSD([sQuery(id+"F22.wireOp",EDGE,"E11.top")])],"isStart":true});
            var Q88;
            Q88=makeQuery(id+"F13.boolean.opBoolean","MERGE",EDGE,{"derivedFrom":[makeQuery(id+"F11.opExtrude","CAP_EDGE",EDGE,{"disambiguationData":[OSD([sQuery(id+"F10.wireOp",EDGE,"E5.right")])],"isStart":false}),makeQuery(id+"F13.opExtrude","SWEPT_EDGE",EDGE,{"disambiguationData":[OSD([sQuery(id+"F12.wireOp",EDGE,"E6.bottom"),sQuery(id+"F12.wireOp",EDGE,"E6.left")])]})]});
            var Q89;
            Q89=makeQuery(id+"F25.opExtrude","CAP_FACE",FACE,{"disambiguationData":[OSD([sQuery(id+"F24.wireOp",EDGE,"E12.bottom"),sQuery(id+"F24.wireOp",EDGE,"E12.top"),sQuery(id+"F24.wireOp",EDGE,"E12.left"),sQuery(id+"F24.wireOp",EDGE,"E12.right")])],"isStart":false});
            var Q90;
            Q90=makeQuery(id+"F3.opExtrude","CAP_EDGE",EDGE,{"disambiguationData":[OSD([sQuery(id+"F2.wireOp",EDGE,"E1.top")])],"isStart":true});
            var Q91;
            Q91=makeQuery(id+"F17.opExtrude","CAP_EDGE",EDGE,{"disambiguationData":[OSD([sQuery(id+"F16.wireOp",EDGE,"E8.left")])],"isStart":false});
            var Q92;
            Q92=makeQuery(id+"F17.boolean.opBoolean","MERGE",EDGE,{"derivedFrom":[makeQuery(id+"F15.opExtrude","CAP_EDGE",EDGE,{"disambiguationData":[OSD([sQuery(id+"F14.wireOp",EDGE,"E7.left")])],"isStart":false}),makeQuery(id+"F17.opExtrude","SWEPT_EDGE",EDGE,{"disambiguationData":[OSD([sQuery(id+"F16.wireOp",EDGE,"E8.top"),sQuery(id+"F16.wireOp",EDGE,"E8.left")])]})]});
            var Q93;
            Q93=makeQuery(id+"F23.boolean.opBoolean","MERGE",EDGE,{"derivedFrom":[makeQuery(id+"F21.opExtrude","CAP_EDGE",EDGE,{"disambiguationData":[OSD([sQuery(id+"F20.wireOp",EDGE,"E10.bottom")])],"isStart":false}),makeQuery(id+"F23.opExtrude","SWEPT_EDGE",EDGE,{"disambiguationData":[OSD([sQuery(id+"F22.wireOp",EDGE,"E11.bottom"),sQuery(id+"F22.wireOp",EDGE,"E11.right")])]})]});
            var Q94;
            Q94=makeQuery(id+"F9.opExtrude","CAP_EDGE",EDGE,{"disambiguationData":[OSD([sQuery(id+"F8.wireOp",EDGE,"E4.right")])],"isStart":true});
            var Q95;
            Q95=makeQuery(id+"F21.boolean.opBoolean","MERGE",EDGE,{"derivedFrom":[makeQuery(id+"F19.opExtrude","CAP_EDGE",EDGE,{"disambiguationData":[OSD([sQuery(id+"F18.wireOp",EDGE,"E9.left")])],"isStart":false}),makeQuery(id+"F21.opExtrude","SWEPT_EDGE",EDGE,{"disambiguationData":[OSD([sQuery(id+"F20.wireOp",EDGE,"E10.top"),sQuery(id+"F20.wireOp",EDGE,"E10.left")])]})]});
            var Q96;
            Q96=makeQuery(id+"F13.boolean.opBoolean","MERGE",EDGE,{"derivedFrom":[makeQuery(id+"F11.opExtrude","CAP_EDGE",EDGE,{"disambiguationData":[OSD([sQuery(id+"F10.wireOp",EDGE,"E5.left")])],"isStart":false}),makeQuery(id+"F13.opExtrude","SWEPT_EDGE",EDGE,{"disambiguationData":[OSD([sQuery(id+"F12.wireOp",EDGE,"E6.top"),sQuery(id+"F12.wireOp",EDGE,"E6.left")])]})]});
            var Q97;
            Q97=makeQuery(id+"F25.opExtrude","CAP_EDGE",EDGE,{"disambiguationData":[OSD([sQuery(id+"F24.wireOp",EDGE,"E12.right")])],"isStart":false});
            var Q98;
            Q98=makeQuery(id+"F13.opExtrude","CAP_EDGE",EDGE,{"disambiguationData":[OSD([sQuery(id+"F12.wireOp",EDGE,"E6.right")])],"isStart":true});
            var Q99;
            Q99=makeQuery(id+"F25.opExtrude","CAP_EDGE",EDGE,{"disambiguationData":[OSD([sQuery(id+"F24.wireOp",EDGE,"E12.right")])],"isStart":true});
            var Q100;
            Q100=makeQuery(id+"F23.opExtrude","SWEPT_EDGE",EDGE,{"disambiguationData":[OSD([sQuery(id+"F16.wireOp",EDGE,"E8.top"),sQuery(id+"F18.wireOp",EDGE,"E9.bottom"),sQuery(id+"F18.wireOp",EDGE,"E9.right"),sQuery(id+"F20.wireOp",EDGE,"E10.bottom"),sQuery(id+"F20.wireOp",EDGE,"E10.right"),sQuery(id+"F22.wireOp",EDGE,"E11.top"),sQuery(id+"F22.wireOp",EDGE,"E11.right")])]});
            var Q101;
            Q101=makeQuery(id+"F25.boolean.opBoolean","MERGE",FACE,{"derivedFrom":[makeQuery(id+"F23.boolean.opBoolean","MERGE",FACE,{"derivedFrom":[makeQuery(id+"F21.boolean.opBoolean","MERGE",FACE,{"derivedFrom":[makeQuery(id+"F19.boolean.opBoolean","MERGE",FACE,{"derivedFrom":[makeQuery(id+"F17.boolean.opBoolean","MERGE",FACE,{"derivedFrom":[makeQuery(id+"F15.boolean.opBoolean","MERGE",FACE,{"derivedFrom":[makeQuery(id+"F13.boolean.opBoolean","MERGE",FACE,{"derivedFrom":[makeQuery(id+"F11.boolean.opBoolean","MERGE",FACE,{"derivedFrom":[makeQuery(id+"F9.boolean.opBoolean","MERGE",FACE,{"derivedFrom":[makeQuery(id+"F7.boolean.opBoolean","MERGE",FACE,{"derivedFrom":[makeQuery(id+"F5.boolean.opBoolean","MERGE",FACE,{"derivedFrom":[makeQuery(id+"F3.boolean.opBoolean","MERGE",FACE,{"derivedFrom":[makeQuery(id+"F1.opExtrude","SWEPT_FACE",FACE,{"disambiguationData":[OSD([sQuery(id+"F0.wireOp",EDGE,"E0.bottom")])]}),makeQuery(id+"F3.opExtrude","SWEPT_FACE",FACE,{"disambiguationData":[OSD([sQuery(id+"F2.wireOp",EDGE,"E1.left")])]})]}),makeQuery(id+"F5.opExtrude","SWEPT_FACE",FACE,{"disambiguationData":[OSD([sQuery(id+"F4.wireOp",EDGE,"E2.top")])]})]}),makeQuery(id+"F7.opExtrude","SWEPT_FACE",FACE,{"disambiguationData":[OSD([sQuery(id+"F6.wireOp",EDGE,"E3.left")])]})]}),makeQuery(id+"F9.opExtrude","SWEPT_FACE",FACE,{"disambiguationData":[OSD([sQuery(id+"F8.wireOp",EDGE,"E4.top")])]})]}),makeQuery(id+"F11.opExtrude","SWEPT_FACE",FACE,{"disambiguationData":[OSD([sQuery(id+"F10.wireOp",EDGE,"E5.right")])]})]}),makeQuery(id+"F13.opExtrude","SWEPT_FACE",FACE,{"disambiguationData":[OSD([sQuery(id+"F12.wireOp",EDGE,"E6.bottom")])]})]}),makeQuery(id+"F15.opExtrude","SWEPT_FACE",FACE,{"disambiguationData":[OSD([sQuery(id+"F14.wireOp",EDGE,"E7.left")])]})]}),makeQuery(id+"F17.opExtrude","SWEPT_FACE",FACE,{"disambiguationData":[OSD([sQuery(id+"F16.wireOp",EDGE,"E8.top")])]})]}),makeQuery(id+"F19.opExtrude","SWEPT_FACE",FACE,{"disambiguationData":[OSD([sQuery(id+"F18.wireOp",EDGE,"E9.right")])]})]}),makeQuery(id+"F21.opExtrude","SWEPT_FACE",FACE,{"disambiguationData":[OSD([sQuery(id+"F20.wireOp",EDGE,"E10.bottom")])]})]}),makeQuery(id+"F23.opExtrude","SWEPT_FACE",FACE,{"disambiguationData":[OSD([sQuery(id+"F22.wireOp",EDGE,"E11.right")])]})]}),makeQuery(id+"F25.opExtrude","SWEPT_FACE",FACE,{"disambiguationData":[OSD([sQuery(id+"F24.wireOp",EDGE,"E12.top")])]})]});
            var Q102;
            Q102=makeQuery(id+"F25.boolean.opBoolean","MERGE",FACE,{"derivedFrom":[makeQuery(id+"F23.boolean.opBoolean","MERGE",FACE,{"derivedFrom":[makeQuery(id+"F21.boolean.opBoolean","MERGE",FACE,{"derivedFrom":[makeQuery(id+"F19.boolean.opBoolean","MERGE",FACE,{"derivedFrom":[makeQuery(id+"F17.boolean.opBoolean","MERGE",FACE,{"derivedFrom":[makeQuery(id+"F15.boolean.opBoolean","MERGE",FACE,{"derivedFrom":[makeQuery(id+"F13.boolean.opBoolean","MERGE",FACE,{"derivedFrom":[makeQuery(id+"F11.boolean.opBoolean","MERGE",FACE,{"derivedFrom":[makeQuery(id+"F9.boolean.opBoolean","MERGE",FACE,{"derivedFrom":[makeQuery(id+"F7.boolean.opBoolean","MERGE",FACE,{"derivedFrom":[makeQuery(id+"F5.boolean.opBoolean","MERGE",FACE,{"derivedFrom":[makeQuery(id+"F3.boolean.opBoolean","MERGE",FACE,{"derivedFrom":[makeQuery(id+"F1.opExtrude","SWEPT_FACE",FACE,{"disambiguationData":[OSD([sQuery(id+"F0.wireOp",EDGE,"E0.top")])]}),makeQuery(id+"F3.opExtrude","SWEPT_FACE",FACE,{"disambiguationData":[OSD([sQuery(id+"F2.wireOp",EDGE,"E1.right")])]})]}),makeQuery(id+"F5.opExtrude","SWEPT_FACE",FACE,{"disambiguationData":[OSD([sQuery(id+"F4.wireOp",EDGE,"E2.bottom")])]})]}),makeQuery(id+"F7.opExtrude","SWEPT_FACE",FACE,{"disambiguationData":[OSD([sQuery(id+"F6.wireOp",EDGE,"E3.right")])]})]}),makeQuery(id+"F9.opExtrude","SWEPT_FACE",FACE,{"disambiguationData":[OSD([sQuery(id+"F8.wireOp",EDGE,"E4.bottom")])]})]}),makeQuery(id+"F11.opExtrude","SWEPT_FACE",FACE,{"disambiguationData":[OSD([sQuery(id+"F10.wireOp",EDGE,"E5.left")])]})]}),makeQuery(id+"F13.opExtrude","SWEPT_FACE",FACE,{"disambiguationData":[OSD([sQuery(id+"F12.wireOp",EDGE,"E6.top")])]})]}),makeQuery(id+"F15.opExtrude","SWEPT_FACE",FACE,{"disambiguationData":[OSD([sQuery(id+"F14.wireOp",EDGE,"E7.right")])]})]}),makeQuery(id+"F17.opExtrude","SWEPT_FACE",FACE,{"disambiguationData":[OSD([sQuery(id+"F16.wireOp",EDGE,"E8.bottom")])]})]}),makeQuery(id+"F19.opExtrude","SWEPT_FACE",FACE,{"disambiguationData":[OSD([sQuery(id+"F18.wireOp",EDGE,"E9.left")])]})]}),makeQuery(id+"F21.opExtrude","SWEPT_FACE",FACE,{"disambiguationData":[OSD([sQuery(id+"F20.wireOp",EDGE,"E10.top")])]})]}),makeQuery(id+"F23.opExtrude","SWEPT_FACE",FACE,{"disambiguationData":[OSD([sQuery(id+"F22.wireOp",EDGE,"E11.left")])]})]}),makeQuery(id+"F25.opExtrude","SWEPT_FACE",FACE,{"disambiguationData":[OSD([sQuery(id+"F24.wireOp",EDGE,"E12.bottom")])]})]});
            var Q103;
            Q103=makeQuery(id+"F1.opExtrude","CAP_FACE",FACE,{"disambiguationData":[OSD([sQuery(id+"F0.wireOp",EDGE,"E0.bottom"),sQuery(id+"F0.wireOp",EDGE,"E0.top"),sQuery(id+"F0.wireOp",EDGE,"E0.left"),sQuery(id+"F0.wireOp",EDGE,"E0.right")])],"isStart":true});
            var Q104;
            Q104=makeQuery(id+"F1.opExtrude","SWEPT_FACE",FACE,{"disambiguationData":[OSD([sQuery(id+"F0.wireOp",EDGE,"E0.left")])]});
            var Q105;
            Q105=makeQuery(id+"F1.opExtrude","SWEPT_EDGE",EDGE,{"disambiguationData":[OSD([sQuery(id+"F0.wireOp",EDGE,"E0.top"),sQuery(id+"F0.wireOp",EDGE,"E0.left")])]});
            var Q106;
            Q106=makeQuery(id+"F1.opExtrude","SWEPT_EDGE",EDGE,{"disambiguationData":[OSD([sQuery(id+"F0.wireOp",EDGE,"E0.bottom"),sQuery(id+"F0.wireOp",EDGE,"E0.right")])]});
            var Q107;
            Q107=makeQuery(id+"F1.opExtrude","SWEPT_FACE",FACE,{"disambiguationData":[OSD([sQuery(id+"F0.wireOp",EDGE,"E0.right")])]});
            var Q108;
            Q108=makeQuery(id+"F1.opExtrude","CAP_EDGE",EDGE,{"disambiguationData":[OSD([sQuery(id+"F0.wireOp",EDGE,"E0.bottom")])],"isStart":true});
            var Q109;
            Q109=makeQuery(id+"F1.opExtrude","CAP_EDGE",EDGE,{"disambiguationData":[OSD([sQuery(id+"F0.wireOp",EDGE,"E0.right")])],"isStart":true});
            var Q110;
            Q110=makeQuery(id+"F1.opExtrude","SWEPT_EDGE",EDGE,{"disambiguationData":[OSD([sQuery(id+"F0.wireOp",EDGE,"E0.top"),sQuery(id+"F0.wireOp",EDGE,"E0.right")])]});
            var Q111;
            Q111=makeQuery(id+"F1.opExtrude","CAP_EDGE",EDGE,{"disambiguationData":[OSD([sQuery(id+"F0.wireOp",EDGE,"E0.left")])],"isStart":true});
            var Q112;
            Q112=makeQuery(id+"F1.opExtrude","CAP_EDGE",EDGE,{"disambiguationData":[OSD([sQuery(id+"F0.wireOp",EDGE,"E0.top")])],"isStart":true});
            var Q113;
            Q113=makeQuery(id+"F1.opExtrude","SWEPT_EDGE",EDGE,{"disambiguationData":[OSD([sQuery(id+"F0.wireOp",EDGE,"E0.bottom"),sQuery(id+"F0.wireOp",EDGE,"E0.left")])]});
            fillet(context, id + "F26", {"entities" : qUnion([Q0, Q1, Q2, Q3, Q4, Q5, Q6, Q7, Q8, Q9, Q10, Q11, Q12, Q13, Q14, Q15, Q16, Q17, Q18, Q19, Q20, Q21, Q22, Q23, Q24, Q25, Q26, Q27, Q28, Q29, Q30, Q31, Q32, Q33, Q34, Q35, Q36, Q37, Q38, Q39, Q40, Q41, Q42, Q43, Q44, Q45, Q46, Q47, Q48, Q49, Q50, Q51, Q52, Q53, Q54, Q55, Q56, Q57, Q58, Q59, Q60, Q61, Q62, Q63, Q64, Q65, Q66, Q67, Q68, Q69, Q70, Q71, Q72, Q73, Q74, Q75, Q76, Q77, Q78, Q79, Q80, Q81, Q82, Q83, Q84, Q85, Q86, Q87, Q88, Q89, Q90, Q91, Q92, Q93, Q94, Q95, Q96, Q97, Q98, Q99, Q100, Q101, Q102, Q103, Q104, Q105, Q106, Q107, Q108, Q109, Q110, Q111, Q112, Q113]), "radius" : 4 * mm, "tangentPropagation" : true, "allowEdgeOverflow" : false});
        }
    });
